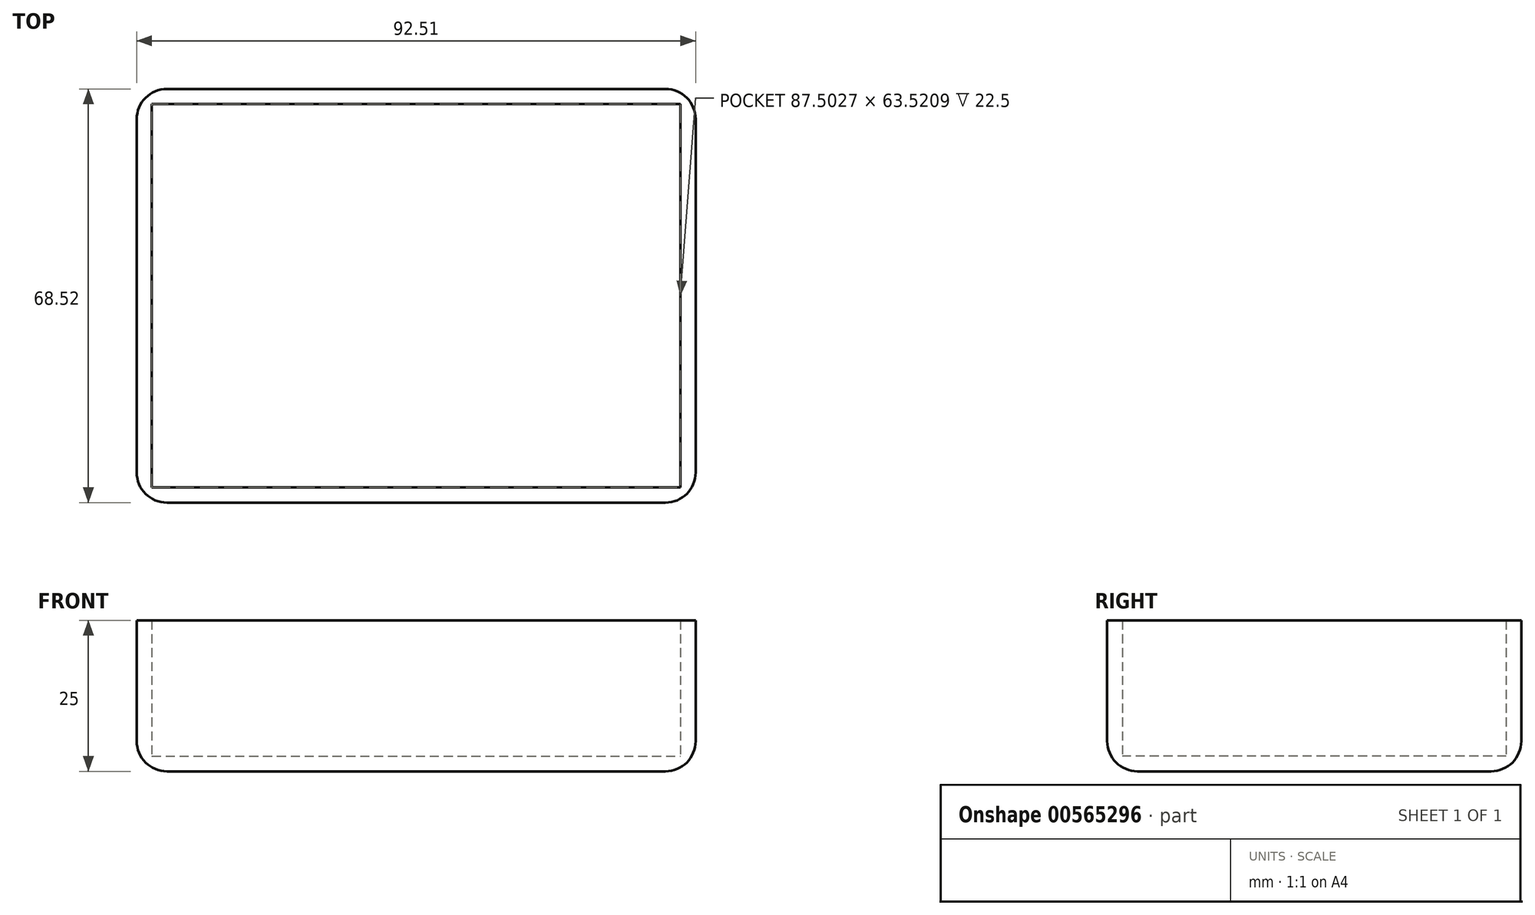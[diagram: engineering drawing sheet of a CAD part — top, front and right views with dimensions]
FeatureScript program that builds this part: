
annotation { "Feature Type Name" : "Feature", "Feature Type Description" : "" }
export const myFeature = defineFeature(function(context is Context, id is Id, definition is map)
    precondition{}
    {
        {
            var Q0;
            Q0=qCreatedBy(makeId("Top.planeOp"),FACE);
            var sketch = newSketch(context, id + "F0", { "sketchPlane" : qUnion([Q0])});
            skLineSegment(sketch, "E0.bottom", {"start": v(-44.45, 35.3) * mm, "end": v(48.06, 35.3) * mm});
            skLineSegment(sketch, "E0.top", {"start": v(-44.45, -33.22) * mm, "end": v(48.06, -33.22) * mm});
            skLineSegment(sketch, "E0.left", {"start": v(-44.45, 35.3) * mm, "end": v(-44.45, -33.22) * mm});
            skLineSegment(sketch, "E0.right", {"start": v(48.06, 35.3) * mm, "end": v(48.06, -33.22) * mm});
            skSolve(sketch);
        }
        {
            var Q0;
            Q0 = qSketchRegion(id + "F0", true);
            extrude(context, id + "F1", {"entities" : qUnion([Q0]), "depth" : 25 * mm, "offsetDistance" : 25 * mm});
        }
        {
            var Q0;
            Q0=makeQuery(id+"F1.opExtrude","CAP_FACE",FACE,{"disambiguationData":[OSD([sQuery(id+"F0.wireOp",EDGE,"E0.bottom"),sQuery(id+"F0.wireOp",EDGE,"E0.top"),sQuery(id+"F0.wireOp",EDGE,"E0.left"),sQuery(id+"F0.wireOp",EDGE,"E0.right")])],"isStart":false});
            shell(context, id + "F2", {"entities" : qUnion([Q0]), "thickness" : 2.5 * mm});
        }
        {
            var Q0;
            Q0=makeQuery(id+"F1.opExtrude","SWEPT_EDGE",EDGE,{"disambiguationData":[OSD([sQuery(id+"F0.wireOp",EDGE,"E0.top"),sQuery(id+"F0.wireOp",EDGE,"E0.right")])]});
            var Q1;
            Q1=makeQuery(id+"F1.opExtrude","SWEPT_EDGE",EDGE,{"disambiguationData":[OSD([sQuery(id+"F0.wireOp",EDGE,"E0.bottom"),sQuery(id+"F0.wireOp",EDGE,"E0.right")])]});
            var Q2;
            Q2=makeQuery(id+"F1.opExtrude","SWEPT_EDGE",EDGE,{"disambiguationData":[OSD([sQuery(id+"F0.wireOp",EDGE,"E0.top"),sQuery(id+"F0.wireOp",EDGE,"E0.left")])]});
            var Q3;
            Q3=makeQuery(id+"F1.opExtrude","SWEPT_EDGE",EDGE,{"disambiguationData":[OSD([sQuery(id+"F0.wireOp",EDGE,"E0.bottom"),sQuery(id+"F0.wireOp",EDGE,"E0.left")])]});
            var Q4;
            Q4=makeQuery(id+"F1.opExtrude","CAP_EDGE",EDGE,{"disambiguationData":[OSD([sQuery(id+"F0.wireOp",EDGE,"E0.bottom")])],"isStart":true});
            var Q5;
            Q5=makeQuery(id+"F1.opExtrude","CAP_EDGE",EDGE,{"disambiguationData":[OSD([sQuery(id+"F0.wireOp",EDGE,"E0.left")])],"isStart":true});
            var Q6;
            Q6=makeQuery(id+"F1.opExtrude","CAP_EDGE",EDGE,{"disambiguationData":[OSD([sQuery(id+"F0.wireOp",EDGE,"E0.top")])],"isStart":true});
            var Q7;
            Q7=makeQuery(id+"F1.opExtrude","CAP_EDGE",EDGE,{"disambiguationData":[OSD([sQuery(id+"F0.wireOp",EDGE,"E0.right")])],"isStart":true});
            fillet(context, id + "F3", {"entities" : qUnion([Q0, Q1, Q2, Q3, Q4, Q5, Q6, Q7]), "radius" : 5 * mm, "tangentPropagation" : true, "allowEdgeOverflow" : false});
        }
    });
